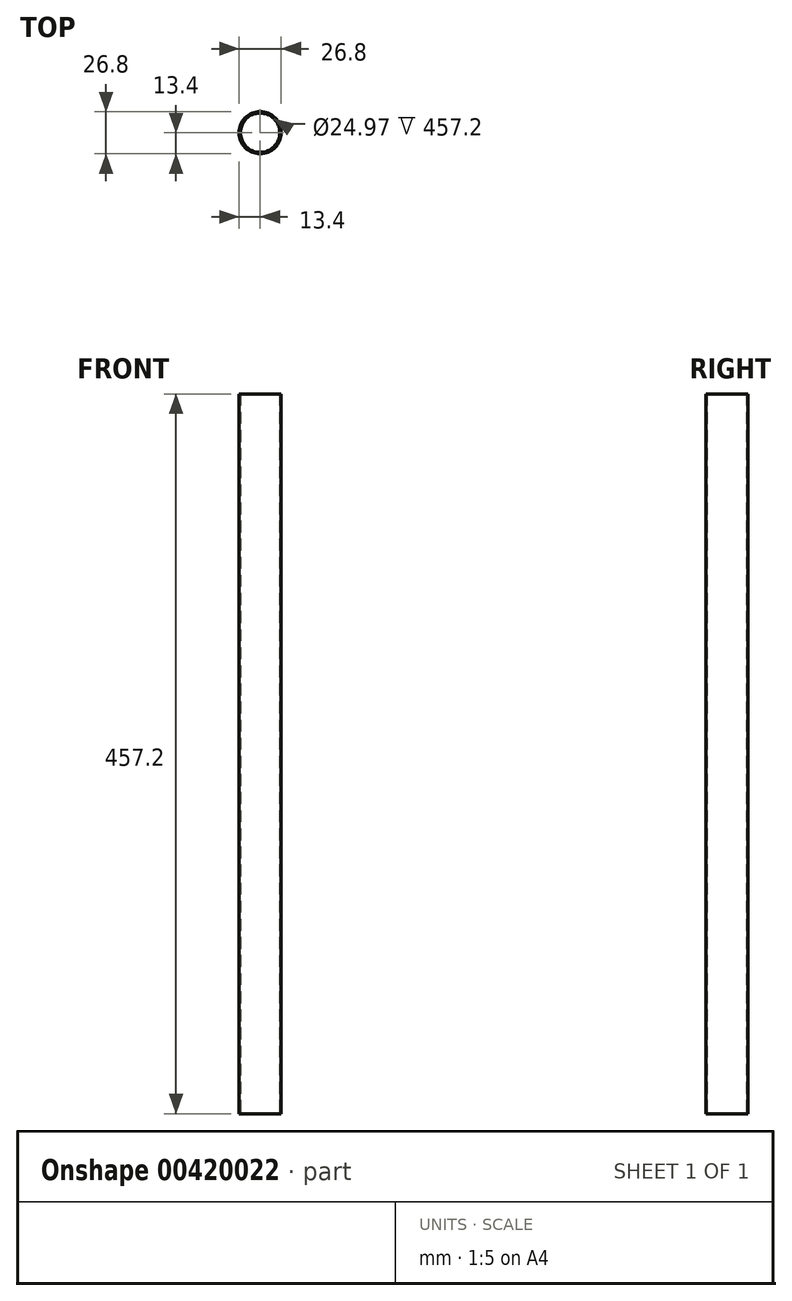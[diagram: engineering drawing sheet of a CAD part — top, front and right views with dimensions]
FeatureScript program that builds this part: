
annotation { "Feature Type Name" : "Feature", "Feature Type Description" : "" }
export const myFeature = defineFeature(function(context is Context, id is Id, definition is map)
    precondition{}
    {
        {
            var Q0;
            Q0=qCreatedBy(makeId("Top.planeOp"),FACE);
            var sketch = newSketch(context, id + "F0", { "sketchPlane" : qUnion([Q0])});
            skCircle(sketch, "E0", {"center": v(0, 0) * mm, "radius": 13.4 * mm});
            skCircle(sketch, "E1", {"center": v(0, 0) * mm, "radius": 12.48 * mm});
            skSolve(sketch);
        }
        {
            var Q0;
            Q0 = qSketchRegion(id + "F0", true);
            extrude(context, id + "F1", {"entities" : qUnion([Q0]), "depth" : 457.2 * mm});
        }
    });
